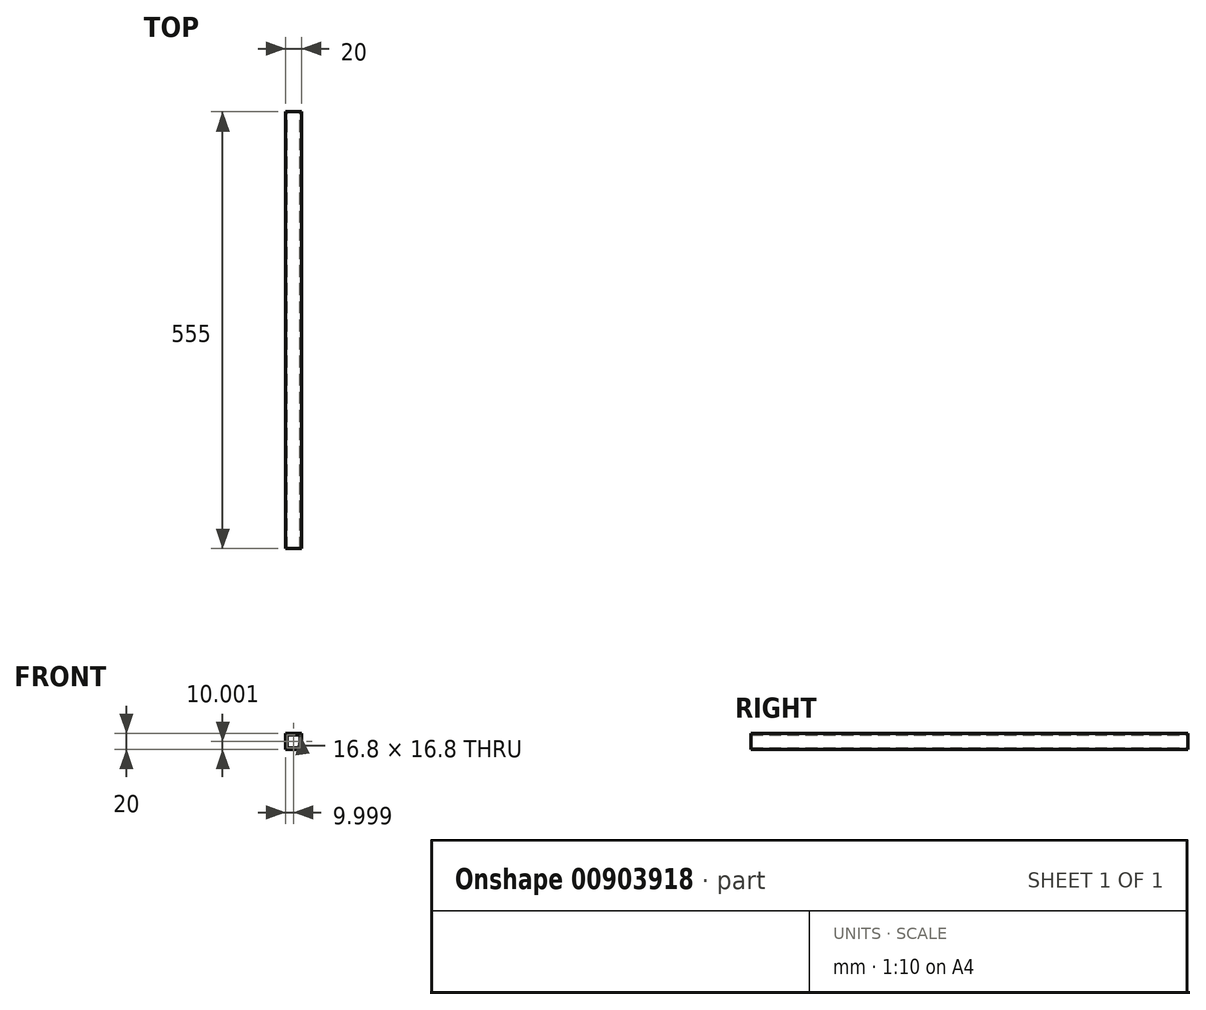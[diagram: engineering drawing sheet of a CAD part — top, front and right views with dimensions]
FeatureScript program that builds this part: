
annotation { "Feature Type Name" : "Feature", "Feature Type Description" : "" }
export const myFeature = defineFeature(function(context is Context, id is Id, definition is map)
    precondition{}
    {
        {
            var Q0;
            Q0=qCreatedBy(makeId("Front.planeOp"),FACE);
            var sketch = newSketch(context, id + "F0", { "sketchPlane" : qUnion([Q0])});
            skLineSegment(sketch, "E0.bottom", {"start": v(6.74, 26.97) * mm, "end": v(26.74, 26.97) * mm});
            skLineSegment(sketch, "E0.top", {"start": v(6.74, 6.97) * mm, "end": v(26.74, 6.97) * mm});
            skLineSegment(sketch, "E0.left", {"start": v(6.74, 26.97) * mm, "end": v(6.74, 6.97) * mm});
            skLineSegment(sketch, "E0.right", {"start": v(26.74, 26.97) * mm, "end": v(26.74, 6.97) * mm});
            skLineSegment(sketch, "E1.0", {"start": v(8.34, 25.37) * mm, "end": v(25.14, 25.37) * mm});
            skLineSegment(sketch, "E1.1", {"start": v(8.34, 25.37) * mm, "end": v(8.34, 8.57) * mm});
            skLineSegment(sketch, "E1.2", {"start": v(8.34, 8.57) * mm, "end": v(25.14, 8.57) * mm});
            skLineSegment(sketch, "E1.3", {"start": v(25.14, 25.37) * mm, "end": v(25.14, 8.57) * mm});
            skSolve(sketch);
        }
        {
            var Q0;
            Q0=makeQuery(id+"F0.imprint","IMPRINT",FACE,{"disambiguationData":[TD([[makeQuery(id+"F0.imprint","IMPRINT",EDGE,{"derivedFrom":sQuery(id+"F0.wireOp",EDGE,"E0.bottom")}),-1.0]])]});
            extrude(context, id + "F1", {"entities" : qUnion([Q0]), "depth" : 555 * mm, "offsetDistance" : 25 * mm});
        }
    });
